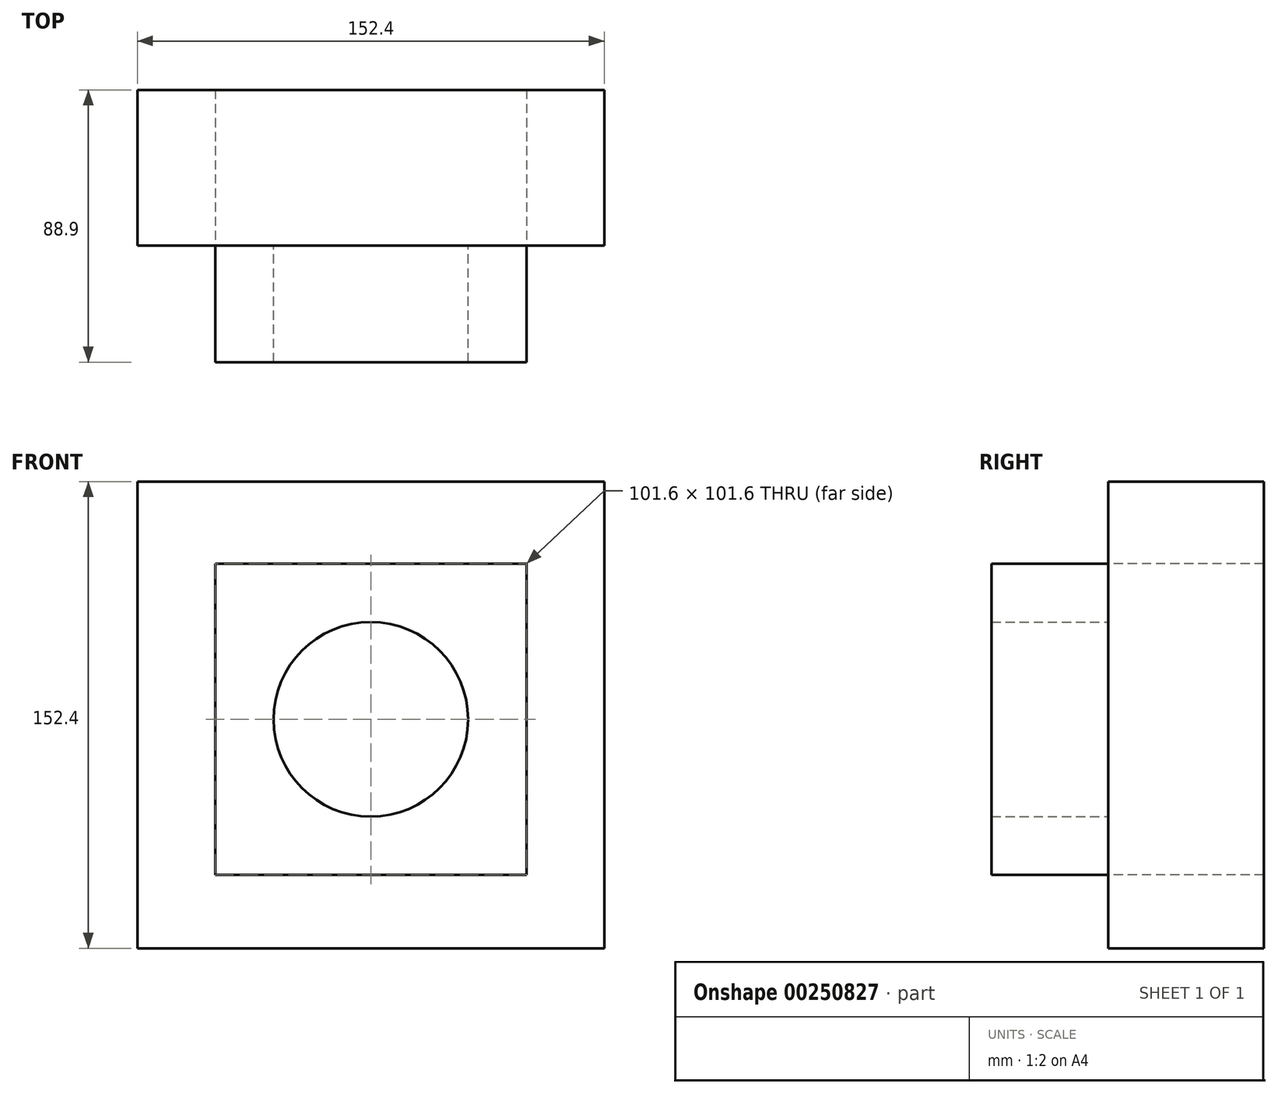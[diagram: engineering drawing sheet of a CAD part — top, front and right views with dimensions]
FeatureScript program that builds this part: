
annotation { "Feature Type Name" : "Feature", "Feature Type Description" : "" }
export const myFeature = defineFeature(function(context is Context, id is Id, definition is map)
    precondition{}
    {
        {
            var Q0;
            Q0=qCreatedBy(makeId("Front.planeOp"),FACE);
            var sketch = newSketch(context, id + "F0", { "sketchPlane" : qUnion([Q0])});
            skCircle(sketch, "E0", {"center": v(0, 0) * mm, "radius": 31.75 * mm});
            skLineSegment(sketch, "E1.bottom", {"start": v(-50.8, 50.8) * mm, "end": v(50.8, 50.8) * mm});
            skLineSegment(sketch, "E1.top", {"start": v(-50.8, -50.8) * mm, "end": v(50.8, -50.8) * mm});
            skLineSegment(sketch, "E1.left", {"start": v(-50.8, 50.8) * mm, "end": v(-50.8, -50.8) * mm});
            skLineSegment(sketch, "E1.right", {"start": v(50.8, 50.8) * mm, "end": v(50.8, -50.8) * mm});
            skLineSegment(sketch, "E2.bottom", {"start": v(76.2, 77.67) * mm, "end": v(-76.2, 77.67) * mm});
            skLineSegment(sketch, "E2.top", {"start": v(76.2, -74.73) * mm, "end": v(-76.2, -74.73) * mm});
            skLineSegment(sketch, "E2.left", {"start": v(76.2, 77.67) * mm, "end": v(76.2, -74.73) * mm});
            skLineSegment(sketch, "E2.right", {"start": v(-76.2, 77.67) * mm, "end": v(-76.2, -74.73) * mm});
            skPoint(sketch, "E2.middle", {"position": v(0, 1.47) * mm});
            skSolve(sketch);
        }
        {
            var Q0;
            Q0=makeQuery(id+"F0.imprint","IMPRINT",FACE,{"disambiguationData":[TD([[makeQuery(id+"F0.imprint","IMPRINT",EDGE,{"derivedFrom":sQuery(id+"F0.wireOp",EDGE,"E0")}),-1.0]])]});
            extrude(context, id + "F1", {"entities" : qUnion([Q0]), "depth" : 38.1 * mm});
        }
        {
            var Q0;
            Q0=makeQuery(id+"F0.imprint","IMPRINT",FACE,{"disambiguationData":[TD([[makeQuery(id+"F0.imprint","IMPRINT",EDGE,{"derivedFrom":sQuery(id+"F0.wireOp",EDGE,"E1.bottom")}),1.0]])]});
            extrude(context, id + "F2", {"entities" : qUnion([Q0]), "oppositeDirection" : true, "depth" : 50.8 * mm});
        }
    });
